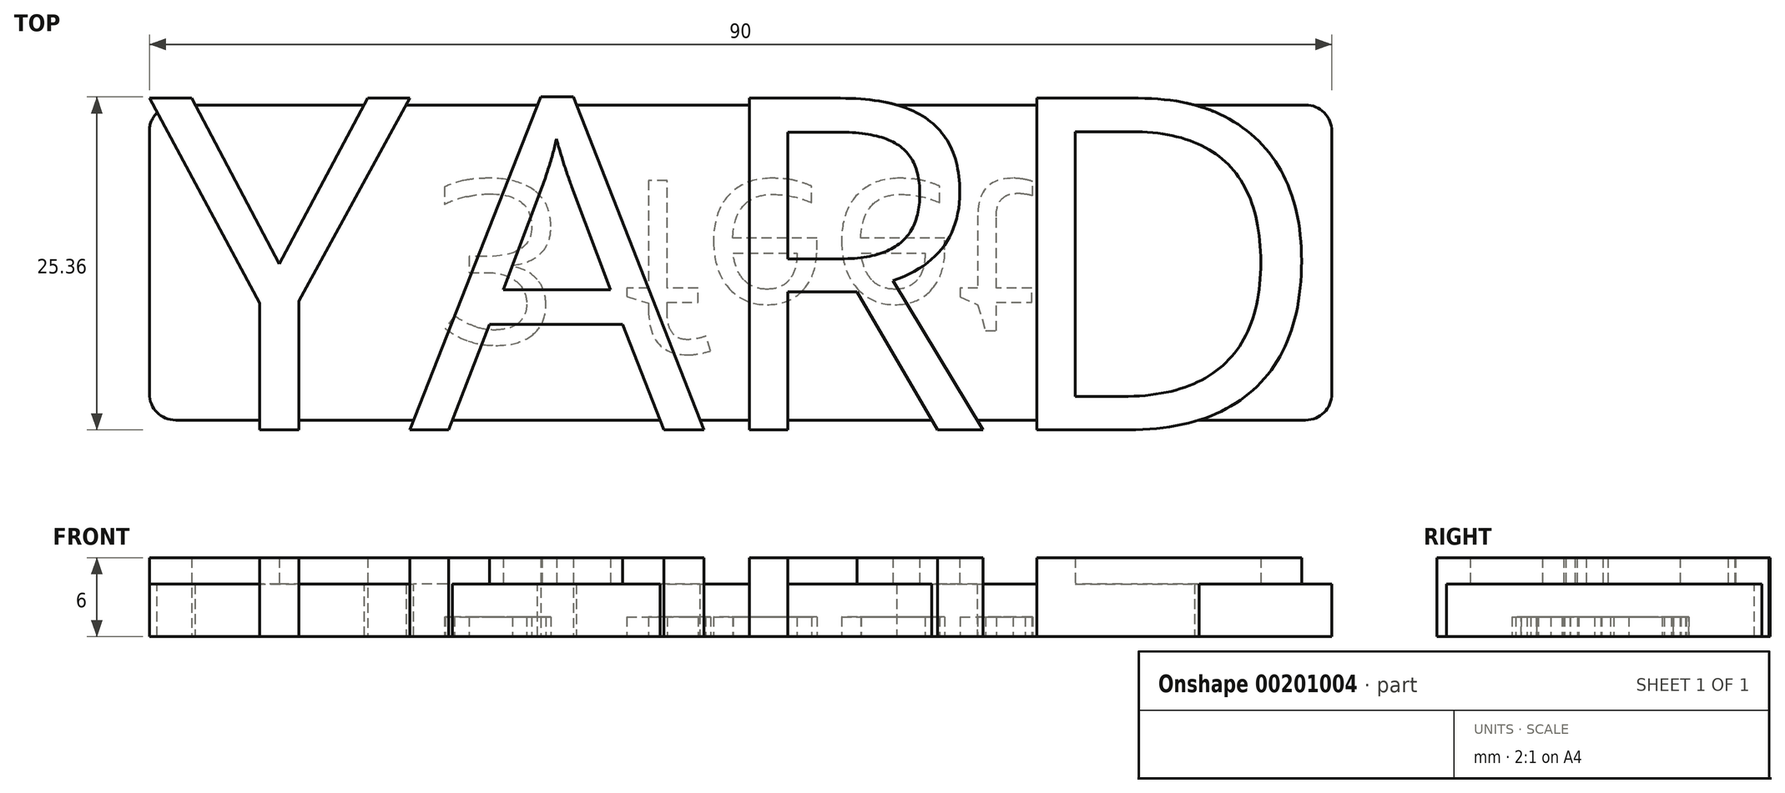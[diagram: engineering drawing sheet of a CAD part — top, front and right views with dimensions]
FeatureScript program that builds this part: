
annotation { "Feature Type Name" : "Feature", "Feature Type Description" : "" }
export const myFeature = defineFeature(function(context is Context, id is Id, definition is map)
    precondition{}
    {
        {
            var Q0;
            Q0=qCreatedBy(makeId("Top.planeOp"),FACE);
            var sketch = newSketch(context, id + "F0", { "sketchPlane" : qUnion([Q0])});
            skLineSegment(sketch, "E0.bottom", {"start": v(-45, 12) * mm, "end": v(45, 12) * mm});
            skLineSegment(sketch, "E0.top", {"start": v(-45, -12) * mm, "end": v(45, -12) * mm});
            skLineSegment(sketch, "E0.left", {"start": v(-45, 12) * mm, "end": v(-45, -12) * mm});
            skLineSegment(sketch, "E0.right", {"start": v(45, 12) * mm, "end": v(45, -12) * mm});
            skLineSegment(sketch, "E1", {"start": v(0, -12) * mm, "end": v(0, 12) * mm, "construction": true});
            skSolve(sketch);
        }
        {
            var Q0;
            Q0=makeQuery(id+"F0.imprint","IMPRINT",FACE,{"disambiguationData":[TD([[makeQuery(id+"F0.imprint","IMPRINT",EDGE,{"derivedFrom":sQuery(id+"F0.wireOp",EDGE,"E0.bottom")}),-1.0]])]});
            extrude(context, id + "F1", {"entities" : qUnion([Q0]), "depth" : 4 * mm});
        }
        {
            var Q0;
            Q0=makeQuery(id+"F1.opExtrude","SWEPT_EDGE",EDGE,{"disambiguationData":[OSD([sQuery(id+"F0.wireOp",EDGE,"E0.top"),sQuery(id+"F0.wireOp",EDGE,"E0.left")])]});
            var Q1;
            Q1=makeQuery(id+"F1.opExtrude","SWEPT_EDGE",EDGE,{"disambiguationData":[OSD([sQuery(id+"F0.wireOp",EDGE,"E0.bottom"),sQuery(id+"F0.wireOp",EDGE,"E0.right")])]});
            var Q2;
            Q2=makeQuery(id+"F1.opExtrude","SWEPT_EDGE",EDGE,{"disambiguationData":[OSD([sQuery(id+"F0.wireOp",EDGE,"E0.bottom"),sQuery(id+"F0.wireOp",EDGE,"E0.left")])]});
            var Q3;
            Q3=makeQuery(id+"F1.opExtrude","SWEPT_EDGE",EDGE,{"disambiguationData":[OSD([sQuery(id+"F0.wireOp",EDGE,"E0.top"),sQuery(id+"F0.wireOp",EDGE,"E0.right")])]});
            fillet(context, id + "F2", {"entities" : qUnion([Q0, Q1, Q2, Q3]), "radius" : 2 * mm, "tangentPropagation" : true, "allowEdgeOverflow" : false});
        }
        {
            var Q0;
            Q0=makeQuery(id+"F1.opExtrude","CAP_FACE",FACE,{"disambiguationData":[OSD([sQuery(id+"F0.wireOp",EDGE,"E0.bottom"),sQuery(id+"F0.wireOp",EDGE,"E0.top"),sQuery(id+"F0.wireOp",EDGE,"E0.left"),sQuery(id+"F0.wireOp",EDGE,"E0.right")])],"isStart":false});
            var sketch = newSketch(context, id + "F3", { "sketchPlane" : qUnion([Q0])});
            skText(sketch, "E2", { "text": "YARD", "fontName": "OpenSans-Regular.ttf"});
            const initialGuessF3  = {"E2": [-0.045, -0.01274, 1, 0, 0.02547]};
            skSetInitialGuess(sketch, initialGuessF3);
            skSolve(sketch);
        }
        {
            var Q0;
            {var subQ0=sQuery(id+"F3.wireOp",EDGE,"E2.sketch_text.stroke-4");Q0=makeQuery(id+"F3.imprint","IMPRINT",FACE,{"disambiguationData":[TD([[makeQuery(id+"F3.imprint","IMPRINT",EDGE,{"derivedFrom":subQ0}),-1.0]])]});}
            var Q1;
            {var subQ0=sQuery(id+"F3.wireOp",EDGE,"E2.sketch_text.stroke-3");var subQ1=sQuery(id+"F3.wireOp",EDGE,"E2.sketch_text.stroke-2");var subQ2=makeQuery(id+"F3.imprint","INTERSECT",VERTEX,{"derivedFrom":[subQ1,subQ0]});Q1=makeQuery(id+"F3.imprint","IMPRINT",FACE,{"disambiguationData":[TD([[makeQuery(id+"F3.imprint","IMPRINT",EDGE,{"disambiguationData":[TD([[subQ2,1.0]])],"derivedFrom":subQ1}),-1.0]])]});}
            var Q2;
            {var subQ1=sQuery(id+"F3.wireOp",EDGE,"E2.sketch_text.stroke-1");Q2=makeQuery(id+"F3.imprint","IMPRINT",FACE,{"disambiguationData":[TD([[makeQuery(id+"F3.imprint","IMPRINT",EDGE,{"derivedFrom":subQ1}),-1.0]])]});}
            var Q3;
            {var subQ0=sQuery(id+"F3.wireOp",EDGE,"E2.sketch_text.stroke-0");var subQ1=makeQuery(id+"F1.opExtrude","CAP_EDGE",EDGE,{"disambiguationData":[OSD([sQuery(id+"F0.wireOp",EDGE,"E0.top")])],"isStart":false});var subQ2=makeQuery(id+"F3.imprint","INTERSECT",VERTEX,{"derivedFrom":[subQ1,subQ0]});Q3=makeQuery(id+"F3.imprint","IMPRINT",FACE,{"disambiguationData":[TD([[makeQuery(id+"F3.imprint","IMPRINT",EDGE,{"disambiguationData":[TD([[subQ2,-1.0]])],"derivedFrom":subQ0}),-1.0]])]});}
            var Q4;
            {var subQ1=sQuery(id+"F3.wireOp",EDGE,"E2.sketch_text.stroke-8");Q4=makeQuery(id+"F3.imprint","IMPRINT",FACE,{"disambiguationData":[TD([[makeQuery(id+"F3.imprint","IMPRINT",EDGE,{"derivedFrom":subQ1}),-1.0]])]});}
            var Q5;
            {var subQ0=sQuery(id+"F3.wireOp",EDGE,"E2.sketch_text.stroke-9");var subQ1=makeQuery(id+"F1.opExtrude","CAP_EDGE",EDGE,{"disambiguationData":[OSD([sQuery(id+"F0.wireOp",EDGE,"E0.bottom")])],"isStart":false});var subQ2=makeQuery(id+"F3.imprint","INTERSECT",VERTEX,{"derivedFrom":[subQ1,subQ0]});Q5=makeQuery(id+"F3.imprint","IMPRINT",FACE,{"disambiguationData":[TD([[makeQuery(id+"F3.imprint","IMPRINT",EDGE,{"disambiguationData":[TD([[subQ2,1.0]])],"derivedFrom":subQ0}),-1.0]])]});}
            var Q6;
            {var subQ1=sQuery(id+"F3.wireOp",EDGE,"E2.sketch_text.stroke-10");Q6=makeQuery(id+"F3.imprint","IMPRINT",FACE,{"disambiguationData":[TD([[makeQuery(id+"F3.imprint","IMPRINT",EDGE,{"derivedFrom":subQ1}),-1.0]])]});}
            var Q7;
            {var subQ0=sQuery(id+"F3.wireOp",EDGE,"E2.sketch_text.stroke-11");var subQ1=makeQuery(id+"F1.opExtrude","CAP_EDGE",EDGE,{"disambiguationData":[OSD([sQuery(id+"F0.wireOp",EDGE,"E0.bottom")])],"isStart":false});var subQ2=makeQuery(id+"F3.imprint","INTERSECT",VERTEX,{"derivedFrom":[subQ1,subQ0]});Q7=makeQuery(id+"F3.imprint","IMPRINT",FACE,{"disambiguationData":[TD([[makeQuery(id+"F3.imprint","IMPRINT",EDGE,{"disambiguationData":[TD([[subQ2,-1.0]])],"derivedFrom":subQ0}),-1.0]])]});}
            var Q8;
            {var subQ0=sQuery(id+"F3.wireOp",EDGE,"E2.sketch_text.stroke-12");Q8=makeQuery(id+"F3.imprint","IMPRINT",FACE,{"disambiguationData":[TD([[makeQuery(id+"F3.imprint","IMPRINT",EDGE,{"derivedFrom":subQ0}),-1.0]])]});}
            var Q9;
            {var subQ0=sQuery(id+"F3.wireOp",EDGE,"E2.sketch_text.stroke-21");Q9=makeQuery(id+"F3.imprint","IMPRINT",FACE,{"disambiguationData":[TD([[makeQuery(id+"F3.imprint","IMPRINT",EDGE,{"derivedFrom":subQ0}),-1.0]])]});}
            var Q10;
            {var subQ0=sQuery(id+"F3.wireOp",EDGE,"E2.sketch_text.stroke-18");var subQ1=makeQuery(id+"F1.opExtrude","CAP_EDGE",EDGE,{"disambiguationData":[OSD([sQuery(id+"F0.wireOp",EDGE,"E0.top")])],"isStart":false});var subQ2=makeQuery(id+"F3.imprint","INTERSECT",VERTEX,{"derivedFrom":[subQ1,subQ0]});Q10=makeQuery(id+"F3.imprint","IMPRINT",FACE,{"disambiguationData":[TD([[makeQuery(id+"F3.imprint","IMPRINT",EDGE,{"disambiguationData":[TD([[subQ2,-1.0]])],"derivedFrom":subQ0}),-1.0]])]});}
            var Q11;
            {var subQ0=sQuery(id+"F3.wireOp",EDGE,"E2.sketch_text.stroke-19");Q11=makeQuery(id+"F3.imprint","IMPRINT",FACE,{"disambiguationData":[TD([[makeQuery(id+"F3.imprint","IMPRINT",EDGE,{"derivedFrom":subQ0}),-1.0]])]});}
            var Q12;
            {var subQ0=sQuery(id+"F3.wireOp",EDGE,"E2.sketch_text.stroke-25");Q12=makeQuery(id+"F3.imprint","IMPRINT",FACE,{"disambiguationData":[TD([[makeQuery(id+"F3.imprint","IMPRINT",EDGE,{"derivedFrom":subQ0}),-1.0]])]});}
            var Q13;
            {var subQ0=sQuery(id+"F3.wireOp",EDGE,"E2.sketch_text.stroke-22");var subQ1=makeQuery(id+"F1.opExtrude","CAP_EDGE",EDGE,{"disambiguationData":[OSD([sQuery(id+"F0.wireOp",EDGE,"E0.top")])],"isStart":false});var subQ2=makeQuery(id+"F3.imprint","INTERSECT",VERTEX,{"derivedFrom":[subQ1,subQ0]});Q13=makeQuery(id+"F3.imprint","IMPRINT",FACE,{"disambiguationData":[TD([[makeQuery(id+"F3.imprint","IMPRINT",EDGE,{"disambiguationData":[TD([[subQ2,-1.0]])],"derivedFrom":subQ0}),-1.0]])]});}
            var Q14;
            {var subQ0=sQuery(id+"F3.wireOp",EDGE,"E2.sketch_text.stroke-23");Q14=makeQuery(id+"F3.imprint","IMPRINT",FACE,{"disambiguationData":[TD([[makeQuery(id+"F3.imprint","IMPRINT",EDGE,{"derivedFrom":subQ0}),-1.0]])]});}
            var Q15;
            {var subQ5=sQuery(id+"F3.wireOp",EDGE,"E2.sketch_text.stroke-28");Q15=makeQuery(id+"F3.imprint","IMPRINT",FACE,{"disambiguationData":[TD([[makeQuery(id+"F3.imprint","IMPRINT",EDGE,{"derivedFrom":subQ5}),-1.0]])]});}
            var Q16;
            {var subQ0=sQuery(id+"F3.wireOp",EDGE,"E2.sketch_text.stroke-34");Q16=makeQuery(id+"F3.imprint","IMPRINT",FACE,{"disambiguationData":[TD([[makeQuery(id+"F3.imprint","IMPRINT",EDGE,{"derivedFrom":subQ0}),-1.0]])]});}
            var Q17;
            {var subQ0=sQuery(id+"F3.wireOp",EDGE,"E2.sketch_text.stroke-30");Q17=makeQuery(id+"F3.imprint","IMPRINT",FACE,{"disambiguationData":[TD([[makeQuery(id+"F3.imprint","IMPRINT",EDGE,{"derivedFrom":subQ0}),-1.0]])]});}
            var Q18;
            {var subQ0=sQuery(id+"F3.wireOp",EDGE,"E2.sketch_text.stroke-6");Q18=makeQuery(id+"F3.imprint","IMPRINT",FACE,{"disambiguationData":[TD([[makeQuery(id+"F3.imprint","IMPRINT",EDGE,{"derivedFrom":subQ0}),-1.0]])]});}
            var Q19;
            {var subQ0=sQuery(id+"F3.wireOp",EDGE,"E2.sketch_text.stroke-17");Q19=makeQuery(id+"F3.imprint","IMPRINT",FACE,{"disambiguationData":[TD([[makeQuery(id+"F3.imprint","IMPRINT",EDGE,{"derivedFrom":subQ0}),-1.0]])]});}
            var Q20;
            {var subQ0=sQuery(id+"F3.wireOp",EDGE,"E2.sketch_text.stroke-27");Q20=makeQuery(id+"F3.imprint","IMPRINT",FACE,{"disambiguationData":[TD([[makeQuery(id+"F3.imprint","IMPRINT",EDGE,{"derivedFrom":subQ0}),-1.0]])]});}
            var Q21;
            {var subQ1=sQuery(id+"F3.wireOp",EDGE,"E2.sketch_text.stroke-40");Q21=makeQuery(id+"F3.imprint","IMPRINT",FACE,{"disambiguationData":[TD([[makeQuery(id+"F3.imprint","IMPRINT",EDGE,{"derivedFrom":subQ1}),-1.0]])]});}
            var Q22;
            {var subQ0=sQuery(id+"F3.wireOp",EDGE,"E2.sketch_text.stroke-14");Q22=makeQuery(id+"F3.imprint","IMPRINT",FACE,{"disambiguationData":[TD([[makeQuery(id+"F3.imprint","IMPRINT",EDGE,{"derivedFrom":subQ0}),-1.0]])]});}
            var Q23;
            {var subQ0=sQuery(id+"F3.wireOp",EDGE,"E2.sketch_text.stroke-42");Q23=makeQuery(id+"F3.imprint","IMPRINT",FACE,{"disambiguationData":[TD([[makeQuery(id+"F3.imprint","IMPRINT",EDGE,{"derivedFrom":subQ0}),-1.0]])]});}
            var Q24;
            {var subQ0=sQuery(id+"F3.wireOp",EDGE,"E2.sketch_text.stroke-44");Q24=makeQuery(id+"F3.imprint","IMPRINT",FACE,{"disambiguationData":[TD([[makeQuery(id+"F3.imprint","IMPRINT",EDGE,{"derivedFrom":subQ0}),-1.0]])]});}
            extrude(context, id + "F4", {"entities" : qUnion([Q0, Q1, Q2, Q3, Q4, Q5, Q6, Q7, Q8, Q9, Q10, Q11, Q12, Q13, Q14, Q15, Q16, Q17, Q18, Q19, Q20, Q21, Q22, Q23, Q24]), "operationType" : NewBodyOperationType.ADD, "depth" : 2 * mm, "hasSecondDirection" : true, "secondDirectionOppositeDirection" : true, "secondDirectionDepth" : 4 * mm});
        }
        {
            var Q0;
            Q0=makeQuery(id+"F1.opExtrude","CAP_FACE",FACE,{"disambiguationData":[OSD([sQuery(id+"F0.wireOp",EDGE,"E0.bottom"),sQuery(id+"F0.wireOp",EDGE,"E0.top"),sQuery(id+"F0.wireOp",EDGE,"E0.left"),sQuery(id+"F0.wireOp",EDGE,"E0.right")])],"isStart":true});
            var sketch = newSketch(context, id + "F5", { "sketchPlane" : qUnion([Q0])});
            skText(sketch, "E3", { "text": "3 feet", "fontName": "OpenSans-Regular.ttf"});
            const initialGuessF5  = {"E3": [-0.02335, -0.00625, 1, 0, 0.0125]};
            skSetInitialGuess(sketch, initialGuessF5);
            skSolve(sketch);
        }
        {
            var Q0;
            Q0=makeQuery(id+"F5.imprint","IMPRINT",FACE,{"disambiguationData":[TD([[makeQuery(id+"F5.imprint","IMPRINT",EDGE,{"derivedFrom":sQuery(id+"F5.wireOp",EDGE,"E3.sketch_text.stroke-86")}),-1.0]])]});
            var Q1;
            Q1=makeQuery(id+"F5.imprint","IMPRINT",FACE,{"disambiguationData":[TD([[makeQuery(id+"F5.imprint","IMPRINT",EDGE,{"derivedFrom":sQuery(id+"F5.wireOp",EDGE,"E3.sketch_text.stroke-70")}),-1.0]])]});
            var Q2;
            Q2=makeQuery(id+"F5.imprint","IMPRINT",FACE,{"disambiguationData":[TD([[makeQuery(id+"F5.imprint","IMPRINT",EDGE,{"derivedFrom":sQuery(id+"F5.wireOp",EDGE,"E3.sketch_text.stroke-39")}),-1.0]])]});
            var Q3;
            Q3=makeQuery(id+"F5.imprint","IMPRINT",FACE,{"disambiguationData":[TD([[makeQuery(id+"F5.imprint","IMPRINT",EDGE,{"derivedFrom":sQuery(id+"F5.wireOp",EDGE,"E3.sketch_text.stroke-19")}),-1.0]])]});
            var Q4;
            Q4=makeQuery(id+"F5.imprint","IMPRINT",FACE,{"disambiguationData":[TD([[makeQuery(id+"F5.imprint","IMPRINT",EDGE,{"derivedFrom":sQuery(id+"F5.wireOp",EDGE,"E3.sketch_text.stroke-0")}),-1.0]])]});
            var Q5;
            Q5=makeQuery(id+"F5.imprint","IMPRINT",FACE,{"disambiguationData":[TD([[makeQuery(id+"F5.imprint","IMPRINT",EDGE,{"derivedFrom":sQuery(id+"F5.wireOp",EDGE,"E3.sketch_text.stroke-45")}),-1.0]])]});
            extrude(context, id + "F6", {"entities" : qUnion([Q0, Q1, Q2, Q3, Q4, Q5]), "operationType" : NewBodyOperationType.REMOVE, "oppositeDirection" : true, "depth" : 1.5 * mm});
        }
    });
